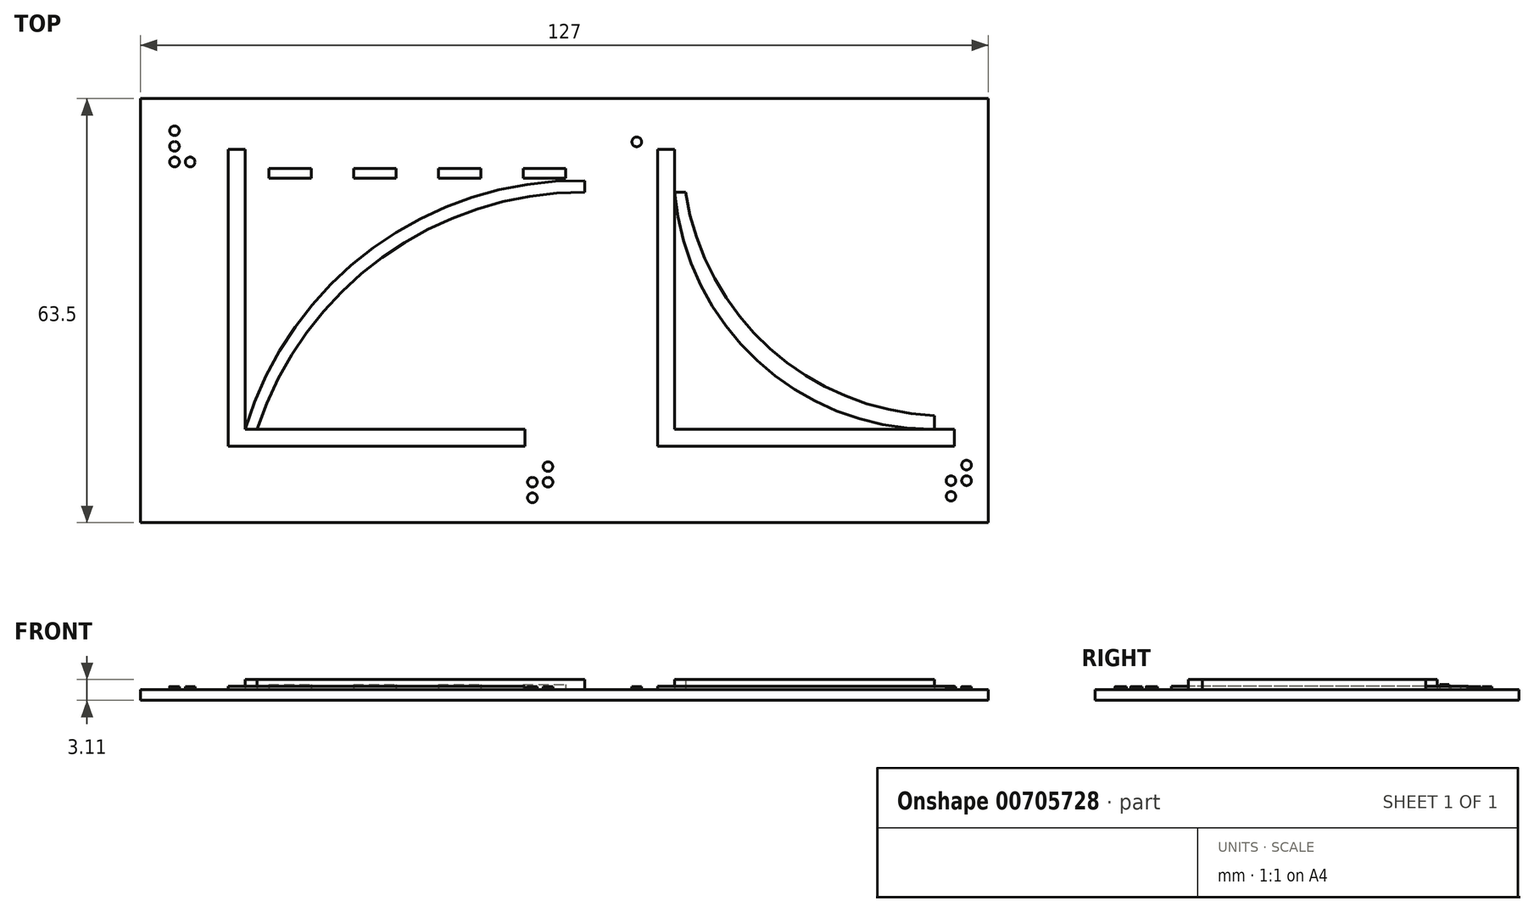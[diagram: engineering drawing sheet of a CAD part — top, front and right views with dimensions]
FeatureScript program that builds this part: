
annotation { "Feature Type Name" : "Feature", "Feature Type Description" : "" }
export const myFeature = defineFeature(function(context is Context, id is Id, definition is map)
    precondition{}
    {
        {
            var Q0;
            Q0=qCreatedBy(makeId("Top.planeOp"),FACE);
            var sketch = newSketch(context, id + "F0", { "sketchPlane" : qUnion([Q0])});
            skLineSegment(sketch, "E0.bottom", {"start": v(0, 0) * mm, "end": v(127, 0) * mm});
            skLineSegment(sketch, "E0.top", {"start": v(0, 63.5) * mm, "end": v(127, 63.5) * mm});
            skLineSegment(sketch, "E0.left", {"start": v(0, 0) * mm, "end": v(0, 63.5) * mm});
            skLineSegment(sketch, "E0.right", {"start": v(127, 0) * mm, "end": v(127, 63.5) * mm});
            skSolve(sketch);
        }
        {
            var Q0;
            Q0=makeQuery(id+"F0.imprint","IMPRINT",FACE,{"disambiguationData":[TD([[makeQuery(id+"F0.imprint","IMPRINT",EDGE,{"derivedFrom":sQuery(id+"F0.wireOp",EDGE,"E0.bottom")}),1.0]])]});
            extrude(context, id + "F1", {"entities" : qUnion([Q0]), "depth" : 1.59 * mm, "offsetDistance" : 25.4 * mm});
        }
        {
            var Q0;
            Q0=makeQuery(id+"F1.opExtrude","CAP_FACE",FACE,{"disambiguationData":[OSD([sQuery(id+"F0.wireOp",EDGE,"E0.bottom"),sQuery(id+"F0.wireOp",EDGE,"E0.top"),sQuery(id+"F0.wireOp",EDGE,"E0.left"),sQuery(id+"F0.wireOp",EDGE,"E0.right")])],"isStart":false});
            var sketch = newSketch(context, id + "F2", { "sketchPlane" : qUnion([Q0])});
            skLineSegment(sketch, "E1.bottom", {"start": v(13.13, 55.88) * mm, "end": v(15.67, 55.88) * mm});
            skLineSegment(sketch, "E1.top", {"start": v(13.13, 11.43) * mm, "end": v(57.58, 11.43) * mm});
            skLineSegment(sketch, "E1.left", {"start": v(13.13, 55.88) * mm, "end": v(13.13, 11.43) * mm});
            skLineSegment(sketch, "E1.right", {"start": v(57.58, 13.97) * mm, "end": v(57.58, 11.43) * mm});
            skLineSegment(sketch, "E2.bottom", {"start": v(77.47, 55.88) * mm, "end": v(80, 55.88) * mm});
            skLineSegment(sketch, "E2.top", {"start": v(77.47, 11.43) * mm, "end": v(121.92, 11.43) * mm});
            skLineSegment(sketch, "E2.left", {"start": v(77.47, 55.88) * mm, "end": v(77.47, 11.43) * mm});
            skLineSegment(sketch, "E2.right", {"start": v(121.92, 13.97) * mm, "end": v(121.92, 11.43) * mm});
            skLineSegment(sketch, "E3.0", {"start": v(15.67, 53.34) * mm, "end": v(15.67, 13.97) * mm});
            skLineSegment(sketch, "E3.3", {"start": v(15.67, 13.97) * mm, "end": v(55.04, 13.97) * mm});
            skLineSegment(sketch, "E4.0", {"start": v(80, 53.34) * mm, "end": v(80, 13.97) * mm});
            skLineSegment(sketch, "E4.3", {"start": v(80, 13.97) * mm, "end": v(119.38, 13.97) * mm});
            skLineSegment(sketch, "E5", {"start": v(15.67, 53.34) * mm, "end": v(15.67, 55.88) * mm});
            skLineSegment(sketch, "E6", {"start": v(55.04, 13.97) * mm, "end": v(57.58, 13.97) * mm});
            skLineSegment(sketch, "E7", {"start": v(119.38, 13.97) * mm, "end": v(121.92, 13.97) * mm});
            skLineSegment(sketch, "E8", {"start": v(80, 53.34) * mm, "end": v(80, 55.88) * mm});
            skSolve(sketch);
        }
        {
            var Q0;
            Q0=makeQuery(id+"F2.imprint","IMPRINT",FACE,{"disambiguationData":[TD([[makeQuery(id+"F2.imprint","IMPRINT",EDGE,{"derivedFrom":sQuery(id+"F2.wireOp",EDGE,"E1.bottom")}),-1.0]])]});
            var Q1;
            Q1=makeQuery(id+"F2.imprint","IMPRINT",FACE,{"disambiguationData":[TD([[makeQuery(id+"F2.imprint","IMPRINT",EDGE,{"derivedFrom":sQuery(id+"F2.wireOp",EDGE,"E2.bottom")}),-1.0]])]});
            extrude(context, id + "F3", {"entities" : qUnion([Q0, Q1]), "operationType" : NewBodyOperationType.ADD, "depth" : 0.5 * mm, "offsetDistance" : 25.4 * mm});
        }
        {
            var Q0;
            Q0=makeQuery(id+"F1.opExtrude","CAP_FACE",FACE,{"disambiguationData":[OSD([sQuery(id+"F0.wireOp",EDGE,"E0.bottom"),sQuery(id+"F0.wireOp",EDGE,"E0.top"),sQuery(id+"F0.wireOp",EDGE,"E0.left"),sQuery(id+"F0.wireOp",EDGE,"E0.right")])],"isStart":false});
            var sketch = newSketch(context, id + "F4", { "sketchPlane" : qUnion([Q0])});
            skLineSegment(sketch, "E9", {"start": v(19.23, 51.6) * mm, "end": v(25.58, 51.6) * mm});
            skLineSegment(sketch, "E10", {"start": v(19.23, 53.04) * mm, "end": v(19.23, 51.6) * mm});
            skLineSegment(sketch, "E11.1.0.0", {"start": v(25.58, 53.04) * mm, "end": v(25.58, 51.6) * mm});
            skLineSegment(sketch, "E11.2.0.0", {"start": v(31.93, 53.04) * mm, "end": v(31.93, 51.6) * mm});
            skLineSegment(sketch, "E11.3.0.0", {"start": v(38.28, 53.04) * mm, "end": v(38.28, 51.6) * mm});
            skLineSegment(sketch, "E11.4.0.0", {"start": v(44.63, 53.04) * mm, "end": v(44.63, 51.6) * mm});
            skLineSegment(sketch, "E11.5.0.0", {"start": v(50.98, 53.04) * mm, "end": v(50.98, 51.6) * mm});
            skLineSegment(sketch, "E11.6.0.0", {"start": v(57.33, 53.04) * mm, "end": v(57.33, 51.6) * mm});
            skLineSegment(sketch, "E11.7.0.0", {"start": v(63.68, 53.04) * mm, "end": v(63.68, 51.6) * mm});
            skLineSegment(sketch, "E11.direction1", {"start": v(19.23, 49.44) * mm, "end": v(25.58, 49.44) * mm, "construction": true});
            skLineSegment(sketch, "E12.direction1", {"start": v(63.68, 49.44) * mm, "end": v(70.03, 49.44) * mm, "construction": true});
            skPoint(sketch, "E13.orphan", {"position": v(15.67, 53.04) * mm});
            skPoint(sketch, "E14.orphan", {"position": v(19.23, 55.1) * mm});
            skPoint(sketch, "E15.orphan", {"position": v(25.58, 55.1) * mm});
            skLineSegment(sketch, "E16.trimOffspring", {"start": v(25.58, 53.04) * mm, "end": v(19.23, 53.04) * mm});
            skLineSegment(sketch, "E17.trimOffspring", {"start": v(31.93, 51.6) * mm, "end": v(38.28, 51.6) * mm});
            skPoint(sketch, "E18.orphan", {"position": v(31.93, 55.1) * mm});
            skPoint(sketch, "E19.orphan", {"position": v(31.93, 49.44) * mm});
            skPoint(sketch, "E20.orphan", {"position": v(38.28, 49.44) * mm});
            skPoint(sketch, "E21.orphan", {"position": v(38.28, 55.1) * mm});
            skLineSegment(sketch, "E22.trimOffspring", {"start": v(38.28, 53.04) * mm, "end": v(31.93, 53.04) * mm});
            skLineSegment(sketch, "E23.trimOffspring", {"start": v(44.63, 51.6) * mm, "end": v(50.98, 51.6) * mm});
            skPoint(sketch, "E24.orphan", {"position": v(44.63, 55.1) * mm});
            skPoint(sketch, "E25.orphan", {"position": v(44.63, 49.44) * mm});
            skPoint(sketch, "E26.orphan", {"position": v(50.98, 49.44) * mm});
            skPoint(sketch, "E27.orphan", {"position": v(50.98, 55.1) * mm});
            skLineSegment(sketch, "E28.trimOffspring", {"start": v(50.98, 53.04) * mm, "end": v(44.63, 53.04) * mm});
            skLineSegment(sketch, "E29.trimOffspring", {"start": v(57.33, 51.6) * mm, "end": v(63.68, 51.6) * mm});
            skPoint(sketch, "E30.orphan", {"position": v(57.33, 49.44) * mm});
            skPoint(sketch, "E31.orphan", {"position": v(57.33, 55.1) * mm});
            skPoint(sketch, "E32.orphan", {"position": v(63.68, 55.1) * mm});
            skLineSegment(sketch, "E33.trimOffspring", {"start": v(63.68, 53.04) * mm, "end": v(57.33, 53.04) * mm});
            skPoint(sketch, "E34.orphan", {"position": v(70.03, 55.1) * mm});
            skPoint(sketch, "E35.orphan", {"position": v(76.38, 55.1) * mm});
            skPoint(sketch, "E36.orphan", {"position": v(82.73, 49.44) * mm});
            skPoint(sketch, "E37.orphan", {"position": v(82.73, 55.1) * mm});
            skPoint(sketch, "E38.orphan", {"position": v(89.08, 55.1) * mm});
            skPoint(sketch, "E39.orphan", {"position": v(89.08, 49.44) * mm});
            skPoint(sketch, "E40.orphan", {"position": v(95.43, 55.1) * mm});
            skPoint(sketch, "E41.orphan", {"position": v(95.43, 49.44) * mm});
            skPoint(sketch, "E42.orphan", {"position": v(101.78, 49.44) * mm});
            skPoint(sketch, "E43.orphan", {"position": v(101.78, 55.1) * mm});
            skPoint(sketch, "E44.orphan", {"position": v(108.13, 49.44) * mm});
            skPoint(sketch, "E45.orphan", {"position": v(108.13, 55.1) * mm});
            skPoint(sketch, "E46.orphan", {"position": v(114.48, 55.1) * mm});
            skPoint(sketch, "E47.orphan", {"position": v(114.48, 49.44) * mm});
            skPoint(sketch, "E48.orphan", {"position": v(120.83, 55.1) * mm});
            skPoint(sketch, "E49.orphan", {"position": v(120.83, 49.44) * mm});
            skLineSegment(sketch, "E50.bottom", {"start": v(121.67, 53.04) * mm, "end": v(121.67, 53.04) * mm});
            skLineSegment(sketch, "E50.top", {"start": v(121.67, 51.6) * mm, "end": v(121.67, 51.6) * mm});
            skSolve(sketch);
        }
        {
            var Q0;
            Q0=makeQuery(id+"F4.imprint","IMPRINT",FACE,{"disambiguationData":[TD([[makeQuery(id+"F4.imprint","IMPRINT",EDGE,{"derivedFrom":sQuery(id+"F4.wireOp",EDGE,"bKQH8Ryr-g0Wq-TpxJ-dn7t-yvmWpIn99Tya")}),1.0]])]});
            var Q1;
            Q1=makeQuery(id+"F4.imprint","IMPRINT",FACE,{"disambiguationData":[TD([[makeQuery(id+"F4.imprint","IMPRINT",EDGE,{"derivedFrom":sQuery(id+"F4.wireOp",EDGE,"E12.7.0.0")}),1.0]])]});
            var Q2;
            Q2=makeQuery(id+"F4.imprint","IMPRINT",FACE,{"disambiguationData":[TD([[makeQuery(id+"F4.imprint","IMPRINT",EDGE,{"derivedFrom":sQuery(id+"F4.wireOp",EDGE,"E12.5.0.0")}),1.0]])]});
            var Q3;
            Q3=makeQuery(id+"F4.imprint","IMPRINT",FACE,{"disambiguationData":[TD([[makeQuery(id+"F4.imprint","IMPRINT",EDGE,{"derivedFrom":sQuery(id+"F4.wireOp",EDGE,"E12.3.0.0")}),1.0]])]});
            var Q4;
            Q4=makeQuery(id+"F4.imprint","IMPRINT",FACE,{"disambiguationData":[TD([[makeQuery(id+"F4.imprint","IMPRINT",EDGE,{"derivedFrom":sQuery(id+"F4.wireOp",EDGE,"E11.6.0.0")}),1.0]])]});
            var Q5;
            Q5=makeQuery(id+"F4.imprint","IMPRINT",FACE,{"disambiguationData":[TD([[makeQuery(id+"F4.imprint","IMPRINT",EDGE,{"derivedFrom":sQuery(id+"F4.wireOp",EDGE,"E11.4.0.0")}),1.0]])]});
            var Q6;
            Q6=makeQuery(id+"F4.imprint","IMPRINT",FACE,{"disambiguationData":[TD([[makeQuery(id+"F4.imprint","IMPRINT",EDGE,{"derivedFrom":sQuery(id+"F4.wireOp",EDGE,"E11.2.0.0")}),1.0]])]});
            var Q7;
            Q7=makeQuery(id+"F4.imprint","IMPRINT",FACE,{"disambiguationData":[TD([[makeQuery(id+"F4.imprint","IMPRINT",EDGE,{"derivedFrom":sQuery(id+"F4.wireOp",EDGE,"E9")}),1.0]])]});
            extrude(context, id + "F5", {"entities" : qUnion([Q0, Q1, Q2, Q3, Q4, Q5, Q6, Q7]), "operationType" : NewBodyOperationType.ADD, "depth" : 0.76 * mm, "offsetDistance" : 25.4 * mm});
        }
        {
            var Q0;
            Q0=makeQuery(id+"F1.opExtrude","CAP_FACE",FACE,{"disambiguationData":[OSD([sQuery(id+"F0.wireOp",EDGE,"E0.bottom"),sQuery(id+"F0.wireOp",EDGE,"E0.top"),sQuery(id+"F0.wireOp",EDGE,"E0.left"),sQuery(id+"F0.wireOp",EDGE,"E0.right")])],"isStart":false});
            var sketch = newSketch(context, id + "F6", { "sketchPlane" : qUnion([Q0])});
            skArc(sketch, "E51", {"start": v(66.52, 51.22) * mm, "mid": v(34.84, 41.14) * mm, "end": v(15.67, 13.97) * mm});
            skLineSegment(sketch, "E52", {"start": v(66.52, 51.22) * mm, "end": v(66.52, 49.51) * mm});
            skArc(sketch, "E53", {"start": v(66.52, 49.51) * mm, "mid": v(36.21, 39.73) * mm, "end": v(17.49, 13.97) * mm});
            skArc(sketch, "E54", {"start": v(80, 49.51) * mm, "mid": v(92.54, 24.13) * mm, "end": v(118.95, 13.97) * mm});
            skLineSegment(sketch, "E55", {"start": v(118.95, 13.97) * mm, "end": v(118.95, 16.05) * mm});
            skArc(sketch, "E56", {"start": v(81.64, 49.51) * mm, "mid": v(94.29, 26.09) * mm, "end": v(118.95, 16.05) * mm});
            skLineSegment(sketch, "E57", {"start": v(80, 49.51) * mm, "end": v(81.64, 49.51) * mm});
            skSolve(sketch);
        }
        {
            var Q0;
            {var subQ1=sQuery(id+"F6.wireOp",EDGE,"E55");Q0=makeQuery(id+"F6.imprint","IMPRINT",FACE,{"disambiguationData":[TD([[makeQuery(id+"F6.imprint","IMPRINT",EDGE,{"derivedFrom":subQ1}),1.0]])]});}
            var Q1;
            {var subQ0=sQuery(id+"F6.wireOp",EDGE,"E51");Q1=makeQuery(id+"F6.imprint","IMPRINT",FACE,{"disambiguationData":[TD([[makeQuery(id+"F6.imprint","IMPRINT",EDGE,{"derivedFrom":subQ0}),1.0]])]});}
            extrude(context, id + "F7", {"entities" : qUnion([Q0, Q1]), "depth" : 1.52 * mm, "offsetDistance" : 25.4 * mm});
        }
        {
            var Q0;
            Q0=makeQuery(id+"F1.opExtrude","CAP_FACE",FACE,{"disambiguationData":[OSD([sQuery(id+"F0.wireOp",EDGE,"E0.bottom"),sQuery(id+"F0.wireOp",EDGE,"E0.top"),sQuery(id+"F0.wireOp",EDGE,"E0.left"),sQuery(id+"F0.wireOp",EDGE,"E0.right")])],"isStart":false});
            var sketch = newSketch(context, id + "F8", { "sketchPlane" : qUnion([Q0])});
            skCircle(sketch, "E58", {"center": v(5.1, 58.7) * mm, "radius": 0.72 * mm});
            skLineSegment(sketch, "E59.direction1", {"start": v(2.4, 58.06) * mm, "end": v(4.74, 58.06) * mm, "construction": true});
            skCircle(sketch, "E60.1.0.0", {"center": v(5.1, 56.36) * mm, "radius": 0.72 * mm});
            skCircle(sketch, "E60.2.0.0", {"center": v(5.1, 54.02) * mm, "radius": 0.72 * mm});
            skCircle(sketch, "E60.2.0.1", {"center": v(7.44, 54.02) * mm, "radius": 0.72 * mm});
            skLineSegment(sketch, "E60.direction1", {"start": v(2.4, 58.06) * mm, "end": v(2.41, 55.72) * mm, "construction": true});
            skCircle(sketch, "E61.1.0.0", {"center": v(61.04, 8.4) * mm, "radius": 0.72 * mm});
            skCircle(sketch, "E62.1.0.0", {"center": v(58.7, 6.07) * mm, "radius": 0.72 * mm});
            skCircle(sketch, "E62.1.0.1", {"center": v(61.05, 6.07) * mm, "radius": 0.72 * mm});
            skCircle(sketch, "E62.2.0.0", {"center": v(58.71, 3.73) * mm, "radius": 0.72 * mm});
            skCircle(sketch, "E63", {"center": v(74.34, 57.03) * mm, "radius": 0.72 * mm});
            skCircle(sketch, "E64.1.0.0", {"center": v(123.74, 8.63) * mm, "radius": 0.72 * mm});
            skCircle(sketch, "E65.1.0.0", {"center": v(121.4, 6.3) * mm, "radius": 0.72 * mm});
            skCircle(sketch, "E65.1.0.1", {"center": v(123.75, 6.3) * mm, "radius": 0.72 * mm});
            skCircle(sketch, "E65.2.0.0", {"center": v(121.41, 3.96) * mm, "radius": 0.72 * mm});
            skPoint(sketch, "E66.2.0.0.center.orphan", {"position": v(72.2, 53.9) * mm});
            skPoint(sketch, "E66.1.0.0.center.orphan", {"position": v(72.2, 56.24) * mm});
            skSolve(sketch);
        }
        {
            var Q0;
            Q0=makeQuery(id+"F8.imprint","IMPRINT",FACE,{"disambiguationData":[TD([[makeQuery(id+"F8.imprint","IMPRINT",EDGE,{"derivedFrom":sQuery(id+"F8.wireOp",EDGE,"E58")}),1.0]])]});
            var Q1;
            Q1=makeQuery(id+"F8.imprint","IMPRINT",FACE,{"disambiguationData":[TD([[makeQuery(id+"F8.imprint","IMPRINT",EDGE,{"derivedFrom":sQuery(id+"F8.wireOp",EDGE,"E60.1.0.0")}),1.0]])]});
            var Q2;
            Q2=makeQuery(id+"F8.imprint","IMPRINT",FACE,{"disambiguationData":[TD([[makeQuery(id+"F8.imprint","IMPRINT",EDGE,{"derivedFrom":sQuery(id+"F8.wireOp",EDGE,"E60.2.0.0")}),1.0]])]});
            var Q3;
            Q3=makeQuery(id+"F8.imprint","IMPRINT",FACE,{"disambiguationData":[TD([[makeQuery(id+"F8.imprint","IMPRINT",EDGE,{"derivedFrom":sQuery(id+"F8.wireOp",EDGE,"E60.2.0.1")}),1.0]])]});
            var Q4;
            Q4=makeQuery(id+"F8.imprint","IMPRINT",FACE,{"disambiguationData":[TD([[makeQuery(id+"F8.imprint","IMPRINT",EDGE,{"derivedFrom":sQuery(id+"F8.wireOp",EDGE,"E62.2.0.0")}),1.0]])]});
            var Q5;
            Q5=makeQuery(id+"F8.imprint","IMPRINT",FACE,{"disambiguationData":[TD([[makeQuery(id+"F8.imprint","IMPRINT",EDGE,{"derivedFrom":sQuery(id+"F8.wireOp",EDGE,"E62.1.0.0")}),1.0]])]});
            var Q6;
            Q6=makeQuery(id+"F8.imprint","IMPRINT",FACE,{"disambiguationData":[TD([[makeQuery(id+"F8.imprint","IMPRINT",EDGE,{"derivedFrom":sQuery(id+"F8.wireOp",EDGE,"E62.1.0.1")}),1.0]])]});
            var Q7;
            Q7=makeQuery(id+"F8.imprint","IMPRINT",FACE,{"disambiguationData":[TD([[makeQuery(id+"F8.imprint","IMPRINT",EDGE,{"derivedFrom":sQuery(id+"F8.wireOp",EDGE,"E61.1.0.0")}),1.0]])]});
            var Q8;
            Q8=makeQuery(id+"F8.imprint","IMPRINT",FACE,{"disambiguationData":[TD([[makeQuery(id+"F8.imprint","IMPRINT",EDGE,{"derivedFrom":sQuery(id+"F8.wireOp",EDGE,"E63")}),1.0]])]});
            var Q9;
            Q9=makeQuery(id+"F8.imprint","IMPRINT",FACE,{"disambiguationData":[TD([[makeQuery(id+"F8.imprint","IMPRINT",EDGE,{"derivedFrom":sQuery(id+"F8.wireOp",EDGE,"E65.2.0.0")}),1.0]])]});
            var Q10;
            Q10=makeQuery(id+"F8.imprint","IMPRINT",FACE,{"disambiguationData":[TD([[makeQuery(id+"F8.imprint","IMPRINT",EDGE,{"derivedFrom":sQuery(id+"F8.wireOp",EDGE,"E65.1.0.0")}),1.0]])]});
            var Q11;
            Q11=makeQuery(id+"F8.imprint","IMPRINT",FACE,{"disambiguationData":[TD([[makeQuery(id+"F8.imprint","IMPRINT",EDGE,{"derivedFrom":sQuery(id+"F8.wireOp",EDGE,"E64.1.0.0")}),1.0]])]});
            var Q12;
            Q12=makeQuery(id+"F8.imprint","IMPRINT",FACE,{"disambiguationData":[TD([[makeQuery(id+"F8.imprint","IMPRINT",EDGE,{"derivedFrom":sQuery(id+"F8.wireOp",EDGE,"E65.1.0.1")}),1.0]])]});
            extrude(context, id + "F9", {"entities" : qUnion([Q0, Q1, Q2, Q3, Q4, Q5, Q6, Q7, Q8, Q9, Q10, Q11, Q12]), "operationType" : NewBodyOperationType.ADD, "depth" : 0.48 * mm, "offsetDistance" : 25.4 * mm});
        }
    });
